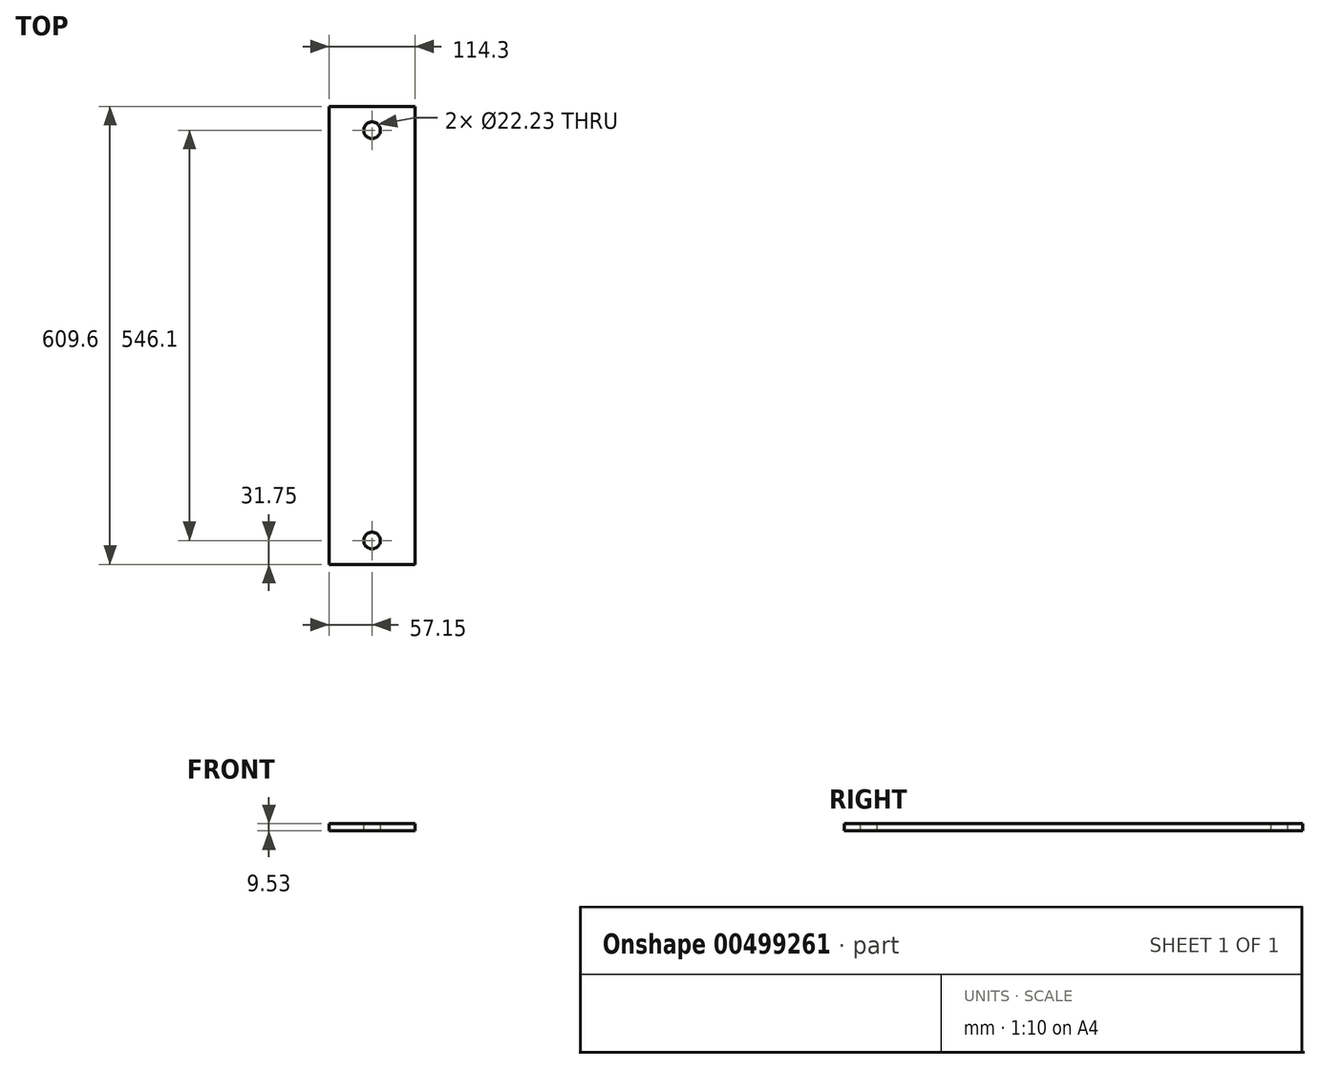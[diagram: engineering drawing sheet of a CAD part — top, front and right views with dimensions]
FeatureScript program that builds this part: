
annotation { "Feature Type Name" : "Feature", "Feature Type Description" : "" }
export const myFeature = defineFeature(function(context is Context, id is Id, definition is map)
    precondition{}
    {
        {
            var Q0;
            Q0=qCreatedBy(makeId("Top.planeOp"),FACE);
            var sketch = newSketch(context, id + "F0", { "sketchPlane" : qUnion([Q0])});
            skLineSegment(sketch, "E0.bottom", {"start": v(57.15, -304.8) * mm, "end": v(-57.15, -304.8) * mm});
            skLineSegment(sketch, "E0.top", {"start": v(57.15, 304.8) * mm, "end": v(-57.15, 304.8) * mm});
            skLineSegment(sketch, "E0.left", {"start": v(57.15, -304.8) * mm, "end": v(57.15, 304.8) * mm});
            skLineSegment(sketch, "E0.right", {"start": v(-57.15, -304.8) * mm, "end": v(-57.15, 304.8) * mm});
            skPoint(sketch, "E0.middle", {"position": v(0, 0) * mm});
            skCircle(sketch, "E1", {"center": v(0, 273.05) * mm, "radius": 11.11 * mm});
            skPoint(sketch, "E1.centerSnap0", {"position": v(0, 304.8) * mm});
            skCircle(sketch, "E2.MirrorC", {"center": v(0, -273.05) * mm, "radius": 11.11 * mm});
            skSolve(sketch);
        }
        {
            var Q0;
            Q0 = qSketchRegion(id + "F0", true);
            extrude(context, id + "F1", {"entities" : qUnion([Q0]), "depth" : 9.52 * mm});
        }
    });
